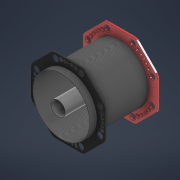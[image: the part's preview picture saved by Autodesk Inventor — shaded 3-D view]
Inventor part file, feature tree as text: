
AUTODESK INVENTOR PART (.ipt)
format: ipt  version: 2022 (Build 260153000, 153)  size: 457,216 bytes
history: native  units: mm
features: hole x12, extrude x7, sketch x6, other x2, fillet x2, plane x2
ambient origin geometry x8: Origin, YZ Plane, XZ Plane, XY Plane, X Axis, Y Axis, Z Axis, Center Point
bodies: Solid1 (feature_tree)
feature tree (31):
  extrude  "Extrusion1"  Depth=416.0mm TaperAngle=0.0deg
  other  "Backplate"
  extrude  "Extrusion2"  Depth=50.0mm TaperAngle=0.0deg
  extrude  "Extrusion3"  Depth=10.0mm
  extrude  "Extrusion4"  Depth=10.0mm
  hole  "Hole1"  [1 undecoded]
  hole  "Hole2"  [1 undecoded]
  hole  "Hole3"  [1 undecoded]
  hole  "Hole4"  [1 undecoded]
  hole  "Hole5"  [1 undecoded]
  fillet  "Fillet1"  Radius=0.5mm
  plane  "Work Plane1"
  extrude  "Extrusion5"  Depth=10.0mm
  fillet  "Fillet2"  Radius=0.5mm
  plane  "Work Plane2"
  other  "Frontplate"
  extrude  "Extrusion6"  Depth=10.0mm
  extrude  "Extrusion7"  [1 undecoded]
  hole  "Hole6"  [1 undecoded]
  hole  "Hole7"  [1 undecoded]
  hole  "Hole8"  [1 undecoded]
  hole  "Hole9"  [1 undecoded]
  hole  "Hole10"  [1 undecoded]
  sketch  "Sketch7"  dims[d29=22.0mm d30=6.0mm d31=4.0mm d32=2.0mm d33=90.0deg d34=8.0mm d35=20.594885mm]
  hole  "Hole11"  [1 undecoded]
  hole  "Hole12"  [1 undecoded]
  sketch  "Sketch1"  dims[d0=14.0mm d1=0.0mm d9=416.0mm d10=0.0mm]
  sketch  "Sketch3"  dims[d11=440.0mm d12=0.0mm d13=50.0mm d14=0.0mm]
  sketch  "Sketch5"  dims[d15=42.0mm d16=6.0mm d17=4.0mm d18=2.0mm d19=90.0deg d20=24.0mm d21=20.594885mm]
  sketch  "Sketch6"  dims[d22=28.0mm d23=6.0mm d24=4.0mm d25=2.0mm d26=90.0deg d27=8.0mm d28=20.594885mm]
  sketch  "Sketch8"  dims[d36=28.0mm d37=6.0mm d38=4.0mm d39=2.0mm d40=90.0deg d41=8.0mm d42=20.594885mm d43=18.0mm d44=6.0mm d45=4.0mm d46=2.0mm d47=90.0deg d48=8.0mm d49=20.594885mm d50=40.0mm d51=360.0mm d52=8.0mm d53=0.0mm d54=40.0mm d55=368.0mm d56=10.0mm d57=0.0mm d58=10.0mm d59=0.0mm d60=42.0mm d61=6.0mm d62=4.0mm d63=2.0mm d64=90.0deg d65=8.0mm d66=20.594885mm d67=28.0mm d68=6.0mm d69=4.0mm d70=2.0mm d71=90.0deg d72=8.0mm d73=20.594885mm d74=22.0mm d75=6.0mm d76=4.0mm d77=2.0mm d78=90.0deg d79=8.0mm d80=20.594885mm d81=18.0mm d82=6.0mm d83=4.0mm d84=2.0mm d85=90.0deg d86=8.0mm d87=20.594885mm d88=3.242mm d89=8.0mm d90=4.0mm d91=2.0mm d92=90.0deg d93=8.0mm d94=0.0mm d95=4.917mm d96=26.0mm d97=4.0mm d98=2.0mm d99=90.0deg d100=30.0mm d101=20.594885mm d102=4.917mm d103=26.0mm d104=4.0mm d105=2.0mm d106=90.0deg d107=30.0mm d108=20.594885mm d2=0.5mm d3=0.872665mm d4=0.5mm d5=0.872665mm]
note: 13 required parameter values undecoded (feature->parameter linkage not recoverable at this tier; creation-order binding heuristic only, values carry confidence <= 0.55)
